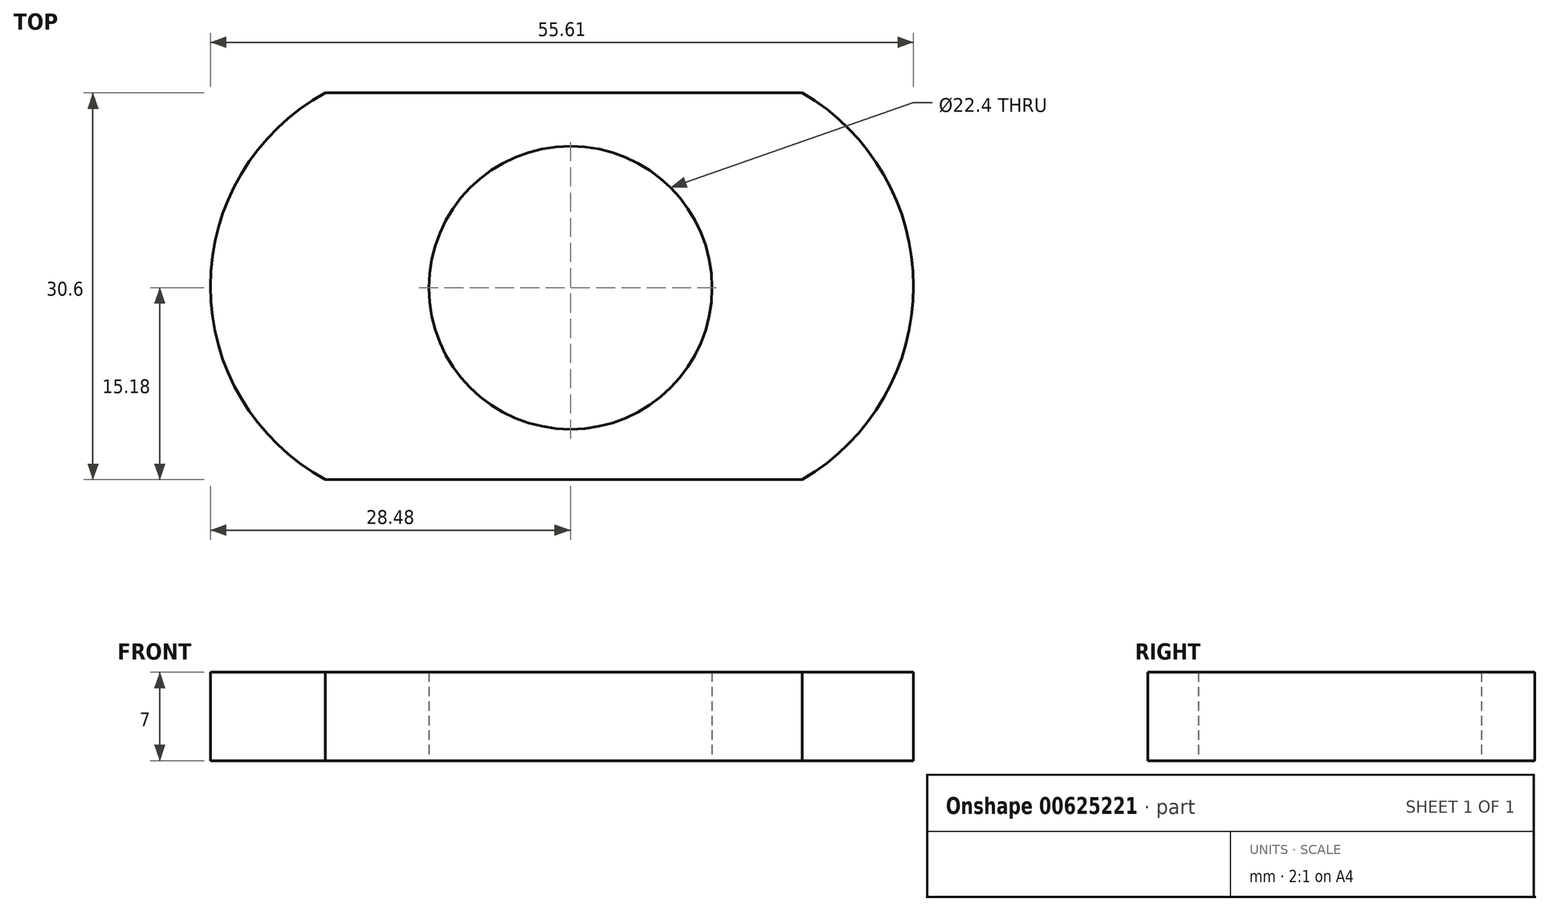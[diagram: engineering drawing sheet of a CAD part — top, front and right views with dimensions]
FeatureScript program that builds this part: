
annotation { "Feature Type Name" : "Feature", "Feature Type Description" : "" }
export const myFeature = defineFeature(function(context is Context, id is Id, definition is map)
    precondition{}
    {
        {
            var Q0;
            Q0=qCreatedBy(makeId("Top.planeOp"),FACE);
            var sketch = newSketch(context, id + "F0", { "sketchPlane" : qUnion([Q0])});
            skCircle(sketch, "E0", {"center": v(0, 0) * mm, "radius": 11.2 * mm});
            skPoint(sketch, "E1.center", {"position": v(-11.2, 0) * mm});
            skArc(sketch, "E2", {"start": v(18.35, -15.18) * mm, "mid": v(27.13, 0.12) * mm, "end": v(18.35, 15.42) * mm});
            skLineSegment(sketch, "E3", {"start": v(18.35, 15.42) * mm, "end": v(-19.38, 15.42) * mm});
            skLineSegment(sketch, "E4", {"start": v(18.35, -15.18) * mm, "end": v(-19.38, -15.18) * mm});
            skArc(sketch, "E5", {"start": v(-19.38, 15.42) * mm, "mid": v(-28.48, 0.12) * mm, "end": v(-19.38, -15.18) * mm});
            skSolve(sketch);
        }
        {
            var Q0;
            Q0=makeQuery(id+"F0.imprint","IMPRINT",FACE,{"disambiguationData":[TD([[makeQuery(id+"F0.imprint","IMPRINT",EDGE,{"derivedFrom":sQuery(id+"F0.wireOp",EDGE,"E0")}),-1.0]])]});
            extrude(context, id + "F1", {"entities" : qUnion([Q0]), "depth" : 7 * mm, "offsetDistance" : 25 * mm});
        }
    });
